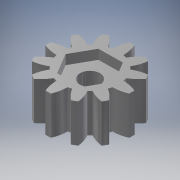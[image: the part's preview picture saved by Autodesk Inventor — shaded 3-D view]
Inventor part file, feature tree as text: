
AUTODESK INVENTOR PART (.ipt)
format: ipt  version: 2017 (Build 210142000, 142)  size: 217,088 bytes
history: native  units: mm (DEFAULTED — no unit token found)
features: sketch x4, extrude x3, plane x3, other x3
ambient origin geometry x8: Origin, YZ Plane, XZ Plane, XY Plane, X Axis, Y Axis, Z Axis, Center Point
bodies: Solid1 (feature_tree)
feature tree (13):
  extrude  "Extrusion1"  Depth=8.0mm TaperAngle=0.0deg
  plane  "Work Plane2"
  plane  "Work Plane8"
  plane  "Work Plane9"
  other  "Spur Gear"
  extrude  "Extrusion2"  Depth=10.0mm TaperAngle=0.0deg
  extrude  "Extrusion3"  TaperAngle=0.0deg  [1 undecoded]
  sketch  "Sketch1"  dims[d0=17.5mm d1=8.0mm d2=0.0mm]
  sketch  "Sketch2"  dims[d3=15.0mm d4=10.0mm d5=0.0mm]
  other  "Srf1"
  sketch  "Sketch3"  dims[d16=31.875mm d17=0.0mm d34=15.0deg]
  sketch  "Sketch4"  dims[d39=0.0mm d41=0.0mm d43=31.875mm d46=31.875mm d47=0.0mm d48=0.0mm d49=4.1656mm d50=10.0mm d51=0.0mm d52=8.7376mm d53=2.0mm d54=0.0mm]
  other  "Pitch Diameter"
note: 1 required parameter value undecoded (feature->parameter linkage not recoverable at this tier; creation-order binding heuristic only, values carry confidence <= 0.55)
